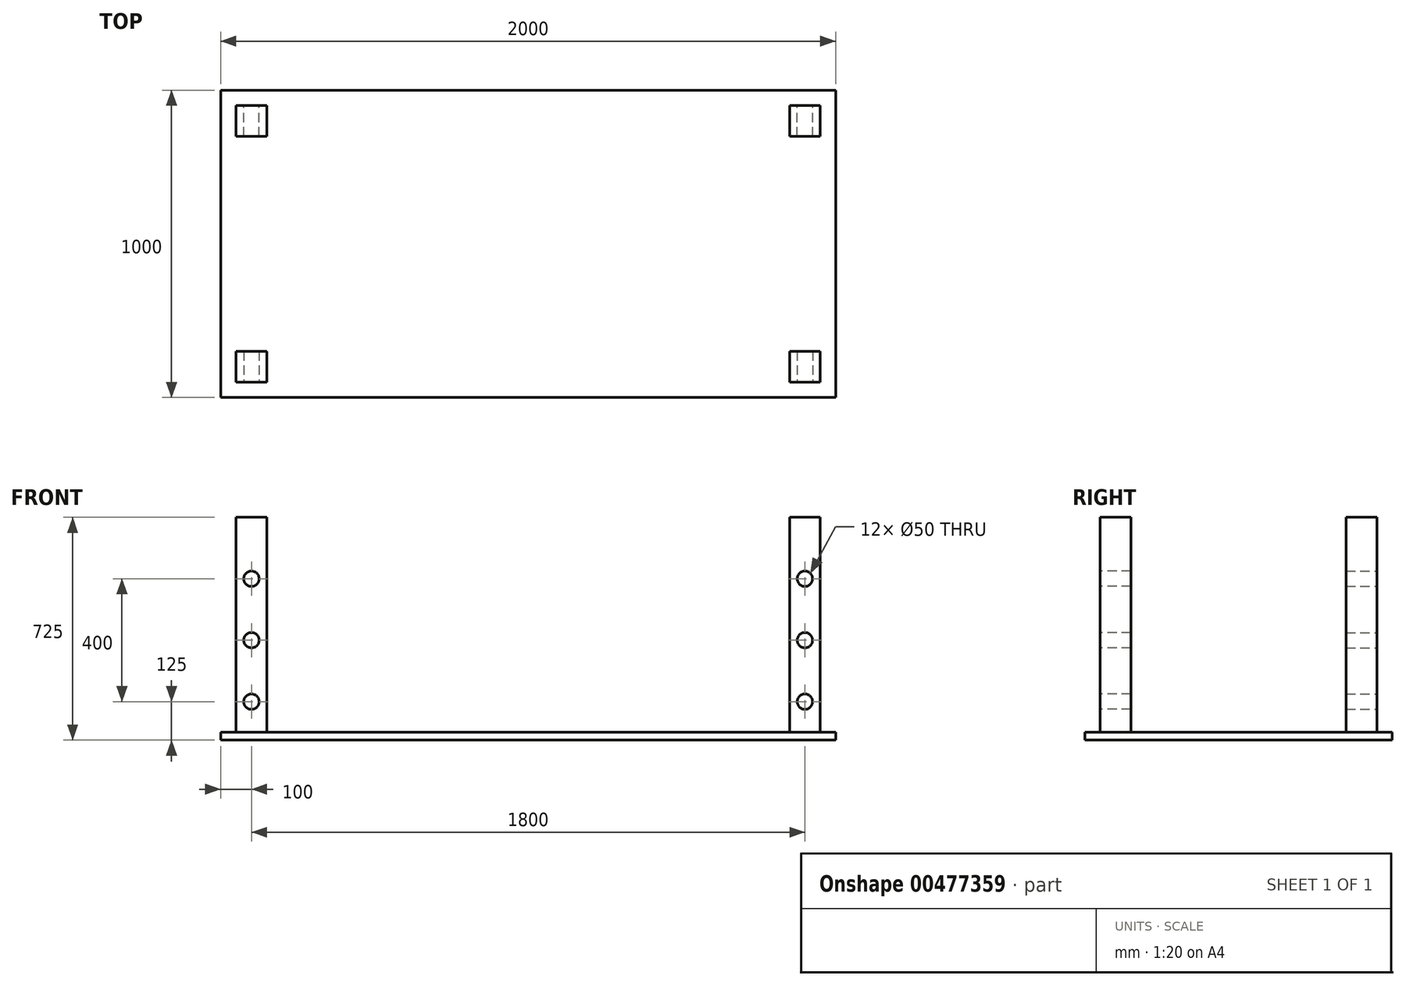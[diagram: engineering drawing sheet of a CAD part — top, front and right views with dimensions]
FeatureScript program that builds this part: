
annotation { "Feature Type Name" : "Feature", "Feature Type Description" : "" }
export const myFeature = defineFeature(function(context is Context, id is Id, definition is map)
    precondition{}
    {
        {
            var Q0;
            Q0=qCreatedBy(makeId("Top.planeOp"),FACE);
            var sketch = newSketch(context, id + "F0", { "sketchPlane" : qUnion([Q0])});
            skLineSegment(sketch, "E0.bottom", {"start": v(-992.2, 418.59) * mm, "end": v(1007.8, 418.59) * mm});
            skLineSegment(sketch, "E0.top", {"start": v(-992.2, -581.41) * mm, "end": v(1007.8, -581.41) * mm});
            skLineSegment(sketch, "E0.left", {"start": v(-992.2, 418.59) * mm, "end": v(-992.2, -581.41) * mm});
            skLineSegment(sketch, "E0.right", {"start": v(1007.8, 418.59) * mm, "end": v(1007.8, -581.41) * mm});
            skSolve(sketch);
        }
        {
            var Q0;
            Q0=makeQuery(id+"F0.imprint","IMPRINT",FACE,{"disambiguationData":[TD([[makeQuery(id+"F0.imprint","IMPRINT",EDGE,{"derivedFrom":sQuery(id+"F0.wireOp",EDGE,"E0.bottom")}),-1.0]])]});
            extrude(context, id + "F1", {"entities" : qUnion([Q0]), "depth" : 25 * mm});
        }
        {
            var Q0;
            Q0=makeQuery(id+"F1.opExtrude","CAP_FACE",FACE,{"disambiguationData":[OSD([sQuery(id+"F0.wireOp",EDGE,"E0.bottom"),sQuery(id+"F0.wireOp",EDGE,"E0.top"),sQuery(id+"F0.wireOp",EDGE,"E0.left"),sQuery(id+"F0.wireOp",EDGE,"E0.right")])],"isStart":false});
            var sketch = newSketch(context, id + "F2", { "sketchPlane" : qUnion([Q0])});
            skLineSegment(sketch, "E1.bottom", {"start": v(-942.2, 368.59) * mm, "end": v(-842.2, 368.59) * mm});
            skLineSegment(sketch, "E1.top", {"start": v(-942.2, 268.59) * mm, "end": v(-842.2, 268.59) * mm});
            skLineSegment(sketch, "E1.left", {"start": v(-942.2, 368.59) * mm, "end": v(-942.2, 268.59) * mm});
            skLineSegment(sketch, "E1.right", {"start": v(-842.2, 368.59) * mm, "end": v(-842.2, 268.59) * mm});
            skSolve(sketch);
        }
        {
            var Q0;
            Q0 = qSketchRegion(id + "F2", true);
            extrude(context, id + "F3", {"entities" : qUnion([Q0]), "operationType" : NewBodyOperationType.ADD, "depth" : 700 * mm});
        }
        {
            var Q0;
            Q0=makeQuery(id+"F3.opExtrude","SWEPT_FACE",FACE,{"disambiguationData":[OSD([sQuery(id+"F2.wireOp",EDGE,"E1.bottom")])]});
            var sketch = newSketch(context, id + "F4", { "sketchPlane" : qUnion([Q0])});
            skCircle(sketch, "E2", {"center": v(892.2, 125) * mm, "radius": 25 * mm});
            skPoint(sketch, "E3.centerSnap0", {"position": v(892.2, 25) * mm});
            skCircle(sketch, "E4", {"center": v(892.2, 325) * mm, "radius": 25 * mm});
            skCircle(sketch, "E5", {"center": v(892.2, 525) * mm, "radius": 25 * mm});
            skSolve(sketch);
        }
        {
            var Q0;
            Q0 = qSketchRegion(id + "F4", true);
            extrude(context, id + "F5", {"entities" : qUnion([Q0]), "operationType" : NewBodyOperationType.REMOVE, "oppositeDirection" : true, "depth" : 100 * mm});
        }
        {
            var Q0;
            Q0=makeQuery(id+"F1.opExtrude","CAP_FACE",FACE,{"disambiguationData":[OSD([sQuery(id+"F0.wireOp",EDGE,"E0.bottom"),sQuery(id+"F0.wireOp",EDGE,"E0.top"),sQuery(id+"F0.wireOp",EDGE,"E0.left"),sQuery(id+"F0.wireOp",EDGE,"E0.right")])],"isStart":false});
            var sketch = newSketch(context, id + "F6", { "sketchPlane" : qUnion([Q0])});
            skLineSegment(sketch, "E6.bottom", {"start": v(857.8, 368.59) * mm, "end": v(957.8, 368.59) * mm});
            skLineSegment(sketch, "E6.top", {"start": v(857.8, 268.59) * mm, "end": v(957.8, 268.59) * mm});
            skLineSegment(sketch, "E6.left", {"start": v(857.8, 368.59) * mm, "end": v(857.8, 268.59) * mm});
            skLineSegment(sketch, "E6.right", {"start": v(957.8, 368.59) * mm, "end": v(957.8, 268.59) * mm});
            skSolve(sketch);
        }
        {
            var Q0;
            Q0 = qSketchRegion(id + "F6", true);
            extrude(context, id + "F7", {"entities" : qUnion([Q0]), "operationType" : NewBodyOperationType.ADD, "depth" : 700 * mm});
        }
        {
            var Q0;
            Q0=makeQuery(id+"F7.opExtrude","SWEPT_FACE",FACE,{"disambiguationData":[OSD([sQuery(id+"F6.wireOp",EDGE,"E6.bottom")])]});
            var sketch = newSketch(context, id + "F8", { "sketchPlane" : qUnion([Q0])});
            skCircle(sketch, "E7", {"center": v(-907.8, 125) * mm, "radius": 25 * mm});
            skCircle(sketch, "E8", {"center": v(-907.8, 325) * mm, "radius": 25 * mm});
            skCircle(sketch, "E9", {"center": v(-907.8, 525) * mm, "radius": 25 * mm});
            skSolve(sketch);
        }
        {
            var Q0;
            Q0 = qSketchRegion(id + "F8", true);
            extrude(context, id + "F9", {"entities" : qUnion([Q0]), "operationType" : NewBodyOperationType.REMOVE, "oppositeDirection" : true, "depth" : 100 * mm});
        }
        {
            var Q0;
            Q0=makeQuery(id+"F1.opExtrude","CAP_FACE",FACE,{"disambiguationData":[OSD([sQuery(id+"F0.wireOp",EDGE,"E0.bottom"),sQuery(id+"F0.wireOp",EDGE,"E0.top"),sQuery(id+"F0.wireOp",EDGE,"E0.left"),sQuery(id+"F0.wireOp",EDGE,"E0.right")])],"isStart":false});
            var sketch = newSketch(context, id + "F10", { "sketchPlane" : qUnion([Q0])});
            skLineSegment(sketch, "E10.bottom", {"start": v(-942.2, -431.41) * mm, "end": v(-842.2, -431.41) * mm});
            skLineSegment(sketch, "E10.top", {"start": v(-942.2, -531.41) * mm, "end": v(-842.2, -531.41) * mm});
            skLineSegment(sketch, "E10.left", {"start": v(-942.2, -431.41) * mm, "end": v(-942.2, -531.41) * mm});
            skLineSegment(sketch, "E10.right", {"start": v(-842.2, -431.41) * mm, "end": v(-842.2, -531.41) * mm});
            skSolve(sketch);
        }
        {
            var Q0;
            Q0 = qSketchRegion(id + "F10", true);
            extrude(context, id + "F11", {"entities" : qUnion([Q0]), "operationType" : NewBodyOperationType.ADD, "depth" : 700 * mm});
        }
        {
            var Q0;
            Q0=makeQuery(id+"F11.opExtrude","SWEPT_FACE",FACE,{"disambiguationData":[OSD([sQuery(id+"F10.wireOp",EDGE,"E10.top")])]});
            var sketch = newSketch(context, id + "F12", { "sketchPlane" : qUnion([Q0])});
            skCircle(sketch, "E11", {"center": v(-892.2, 525) * mm, "radius": 25 * mm});
            skCircle(sketch, "E12", {"center": v(-892.2, 325) * mm, "radius": 25 * mm});
            skCircle(sketch, "E13", {"center": v(-892.2, 125) * mm, "radius": 25 * mm});
            skSolve(sketch);
        }
        {
            var Q0;
            Q0 = qSketchRegion(id + "F12", true);
            extrude(context, id + "F13", {"entities" : qUnion([Q0]), "operationType" : NewBodyOperationType.REMOVE, "oppositeDirection" : true, "depth" : 100 * mm});
        }
        {
            var Q0;
            Q0=makeQuery(id+"F1.opExtrude","CAP_FACE",FACE,{"disambiguationData":[OSD([sQuery(id+"F0.wireOp",EDGE,"E0.bottom"),sQuery(id+"F0.wireOp",EDGE,"E0.top"),sQuery(id+"F0.wireOp",EDGE,"E0.left"),sQuery(id+"F0.wireOp",EDGE,"E0.right")])],"isStart":false});
            var sketch = newSketch(context, id + "F14", { "sketchPlane" : qUnion([Q0])});
            skLineSegment(sketch, "E14.bottom", {"start": v(857.8, -431.41) * mm, "end": v(957.8, -431.41) * mm});
            skLineSegment(sketch, "E14.top", {"start": v(857.8, -531.41) * mm, "end": v(957.8, -531.41) * mm});
            skLineSegment(sketch, "E14.left", {"start": v(857.8, -431.41) * mm, "end": v(857.8, -531.41) * mm});
            skLineSegment(sketch, "E14.right", {"start": v(957.8, -431.41) * mm, "end": v(957.8, -531.41) * mm});
            skSolve(sketch);
        }
        {
            var Q0;
            Q0 = qSketchRegion(id + "F14", true);
            extrude(context, id + "F15", {"entities" : qUnion([Q0]), "operationType" : NewBodyOperationType.ADD, "depth" : 700 * mm});
        }
        {
            var Q0;
            Q0=makeQuery(id+"F15.opExtrude","SWEPT_FACE",FACE,{"disambiguationData":[OSD([sQuery(id+"F14.wireOp",EDGE,"E14.top")])]});
            var sketch = newSketch(context, id + "F16", { "sketchPlane" : qUnion([Q0])});
            skCircle(sketch, "E15", {"center": v(907.8, 525) * mm, "radius": 25 * mm});
            skCircle(sketch, "E16", {"center": v(907.8, 325) * mm, "radius": 25 * mm});
            skCircle(sketch, "E17", {"center": v(907.8, 125) * mm, "radius": 25 * mm});
            skSolve(sketch);
        }
        {
            var Q0;
            Q0 = qSketchRegion(id + "F16", true);
            extrude(context, id + "F17", {"entities" : qUnion([Q0]), "operationType" : NewBodyOperationType.REMOVE, "oppositeDirection" : true, "depth" : 100 * mm});
        }
    });
